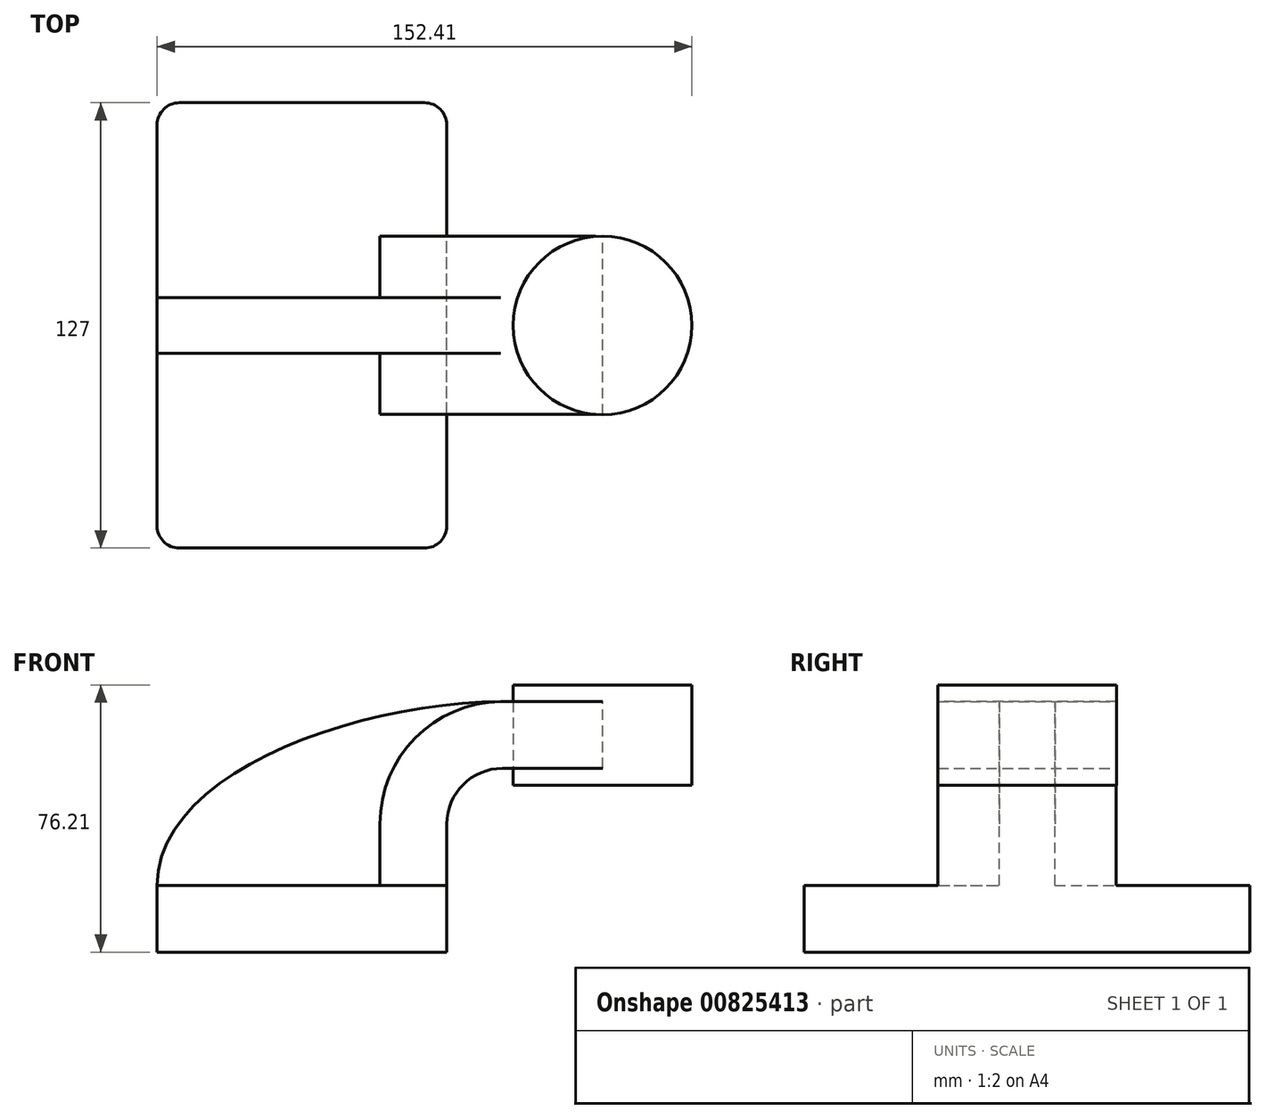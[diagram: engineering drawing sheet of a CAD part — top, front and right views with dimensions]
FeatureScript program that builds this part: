
annotation { "Feature Type Name" : "Feature", "Feature Type Description" : "" }
export const myFeature = defineFeature(function(context is Context, id is Id, definition is map)
    precondition{}
    {
        {
            var Q0;
            Q0=qCreatedBy(makeId("Front.planeOp"),FACE);
            var sketch = newSketch(context, id + "F0", { "sketchPlane" : qUnion([Q0])});
            skLineSegment(sketch, "E0.bottom", {"start": v(41.28, -9.52) * mm, "end": v(-41.28, -9.53) * mm});
            skLineSegment(sketch, "E0.top", {"start": v(41.28, 9.53) * mm, "end": v(-41.28, 9.53) * mm});
            skLineSegment(sketch, "E0.left", {"start": v(41.28, -9.52) * mm, "end": v(41.28, 9.53) * mm});
            skLineSegment(sketch, "E0.right", {"start": v(-41.28, -9.53) * mm, "end": v(-41.28, 9.53) * mm});
            skPoint(sketch, "E0.middle", {"position": v(0, 0) * mm});
            skLineSegment(sketch, "E1.bottom", {"start": v(60.33, 38.1) * mm, "end": v(111.12, 38.1) * mm});
            skLineSegment(sketch, "E1.top", {"start": v(60.32, 66.68) * mm, "end": v(111.12, 66.68) * mm});
            skLineSegment(sketch, "E1.left", {"start": v(60.33, 38.1) * mm, "end": v(60.32, 66.68) * mm});
            skLineSegment(sketch, "E1.right", {"start": v(111.12, 38.1) * mm, "end": v(111.12, 66.68) * mm});
            skPoint(sketch, "E1.middle", {"position": v(85.72, 52.39) * mm});
            skLineSegment(sketch, "E2", {"start": v(41.28, 9.53) * mm, "end": v(41.28, 27) * mm});
            skArc(sketch, "E3", {"start": v(57.15, 42.88) * mm, "mid": v(45.92, 38.23) * mm, "end": v(41.27, 27) * mm});
            skLineSegment(sketch, "E4", {"start": v(57.15, 42.88) * mm, "end": v(85.65, 42.88) * mm});
            skLineSegment(sketch, "E5.0", {"start": v(22.22, 9.53) * mm, "end": v(22.22, 27) * mm});
            skArc(sketch, "E5.1", {"start": v(57.15, 61.93) * mm, "mid": v(32.45, 51.7) * mm, "end": v(22.22, 27) * mm});
            skLineSegment(sketch, "E5.2", {"start": v(57.15, 61.93) * mm, "end": v(85.65, 61.93) * mm});
            skLineSegment(sketch, "E6", {"start": v(85.65, 38.1) * mm, "end": v(85.65, 66.68) * mm});
            skFitSpline(sketch, "E7", {"points": [v(-41.28, 9.53) * mm, v(57.15, 61.93) * mm], "startDerivative": vector(0.63, 98.01) * mm, "endDerivative": vector(123.08, 0.62) * mm});
            skSolve(sketch);
        }
        {
            var Q0;
            Q0=makeQuery(id+"F0.imprint","IMPRINT",FACE,{"disambiguationData":[TD([[makeQuery(id+"F0.imprint","IMPRINT",EDGE,{"derivedFrom":sQuery(id+"F0.wireOp",EDGE,"E0.bottom")}),-1.0]])]});
            extrude(context, id + "F1", {"entities" : qUnion([Q0]), "endBound" : BoundingType.SYMMETRIC, "depth" : 127 * mm, "offsetDistance" : 25.4 * mm});
        }
        {
            var Q0;
            {var subQ1=sQuery(id+"F0.wireOp",EDGE,"E2");Q0=makeQuery(id+"F0.imprint","IMPRINT",FACE,{"disambiguationData":[TD([[makeQuery(id+"F0.imprint","IMPRINT",EDGE,{"derivedFrom":subQ1}),1.0]])]});}
            var Q1;
            {var subQ0=sQuery(id+"F0.wireOp",EDGE,"E4");var subQ1=sQuery(id+"F0.wireOp",EDGE,"E1.left");var subQ2=makeQuery(id+"F0.imprint","INTERSECT",VERTEX,{"derivedFrom":[subQ1,subQ0]});Q1=makeQuery(id+"F0.imprint","IMPRINT",FACE,{"disambiguationData":[TD([[makeQuery(id+"F0.imprint","IMPRINT",EDGE,{"disambiguationData":[TD([[subQ2,-1.0]])],"derivedFrom":subQ1}),-1.0]])]});}
            extrude(context, id + "F2", {"entities" : qUnion([Q0, Q1]), "operationType" : NewBodyOperationType.ADD, "endBound" : BoundingType.SYMMETRIC, "depth" : 50.8 * mm, "offsetDistance" : 25.4 * mm});
        }
        {
            var Q0;
            {var subQ3=sQuery(id+"F0.wireOp",EDGE,"E5.0");Q0=makeQuery(id+"F0.imprint","IMPRINT",FACE,{"disambiguationData":[TD([[makeQuery(id+"F0.imprint","IMPRINT",EDGE,{"derivedFrom":subQ3}),1.0]])]});}
            extrude(context, id + "F3", {"entities" : qUnion([Q0]), "operationType" : NewBodyOperationType.ADD, "endBound" : BoundingType.SYMMETRIC, "depth" : 15.88 * mm, "offsetDistance" : 25.4 * mm});
        }
        {
            var Q0;
            {var subQ4=sQuery(id+"F0.wireOp",EDGE,"E1.right");Q0=makeQuery(id+"F0.imprint","IMPRINT",FACE,{"disambiguationData":[TD([[makeQuery(id+"F0.imprint","IMPRINT",EDGE,{"derivedFrom":subQ4}),1.0]])]});}
            var Q1;
            Q1=sQuery(id+"F0.wireOp",EDGE,"E6");
            revolve(context, id + "F4", {"surfaceOperationType" : NewSurfaceOperationType.NEW, "entities" : qUnion([Q0]), "axis" : qUnion([Q1]), "revolveType" : RevolveType.FULL});
        }
        {
            var Q0;
            Q0=makeQuery(id+"F1.opExtrude","CAP_EDGE",EDGE,{"disambiguationData":[OSD([sQuery(id+"F0.wireOp",EDGE,"E0.right")])],"isStart":false});
            var Q1;
            Q1=makeQuery(id+"F1.opExtrude","CAP_EDGE",EDGE,{"disambiguationData":[OSD([sQuery(id+"F0.wireOp",EDGE,"E0.left")])],"isStart":false});
            var Q2;
            Q2=makeQuery(id+"F1.opExtrude","CAP_EDGE",EDGE,{"disambiguationData":[OSD([sQuery(id+"F0.wireOp",EDGE,"E0.left")])],"isStart":true});
            var Q3;
            Q3=makeQuery(id+"F1.opExtrude","CAP_EDGE",EDGE,{"disambiguationData":[OSD([sQuery(id+"F0.wireOp",EDGE,"E0.right")])],"isStart":true});
            fillet(context, id + "F5", {"entities" : qUnion([Q0, Q1, Q2, Q3]), "radius" : 6.35 * mm, "tangentPropagation" : true, "allowEdgeOverflow" : false});
        }
    });
